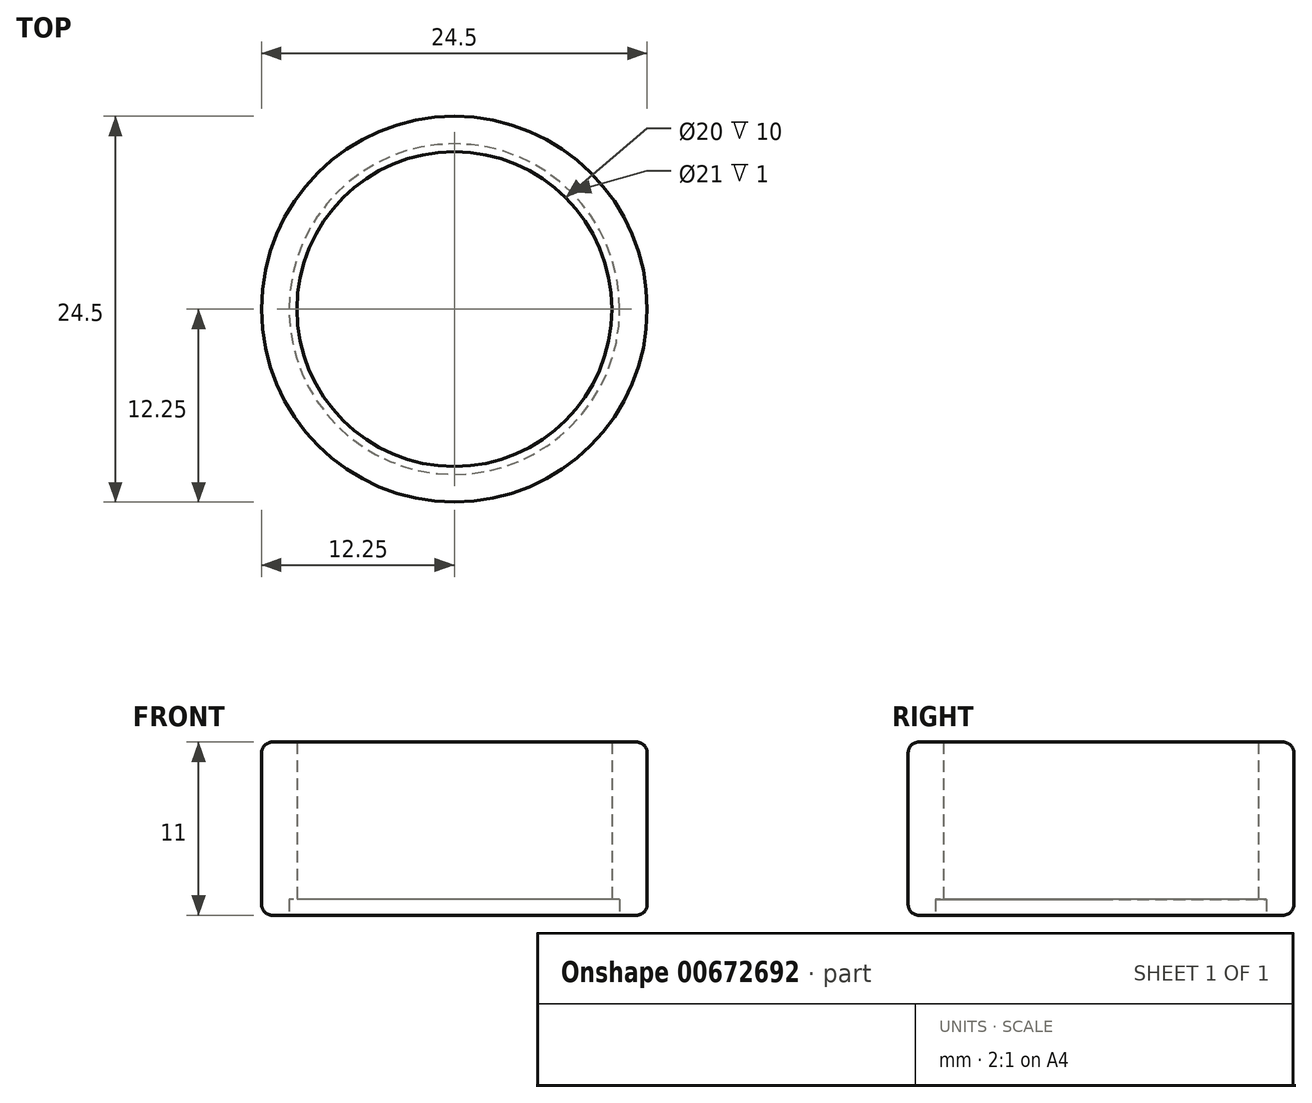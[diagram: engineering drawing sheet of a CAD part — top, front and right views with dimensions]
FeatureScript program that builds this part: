
annotation { "Feature Type Name" : "Feature", "Feature Type Description" : "" }
export const myFeature = defineFeature(function(context is Context, id is Id, definition is map)
    precondition{}
    {
        {
            var Q0;
            Q0=qCreatedBy(makeId("Top.planeOp"),FACE);
            var sketch = newSketch(context, id + "F0", { "sketchPlane" : qUnion([Q0])});
            skCircle(sketch, "E0", {"center": v(0, 0) * mm, "radius": 12.25 * mm});
            skCircle(sketch, "E1", {"center": v(0, 0) * mm, "radius": 10.5 * mm});
            skCircle(sketch, "E2", {"center": v(0, 0) * mm, "radius": 10 * mm});
            skSolve(sketch);
        }
        {
            var Q0;
            Q0=makeQuery(id+"F0.imprint","IMPRINT",FACE,{"disambiguationData":[TD([[makeQuery(id+"F0.imprint","IMPRINT",EDGE,{"derivedFrom":sQuery(id+"F0.wireOp",EDGE,"E0")}),1.0]])]});
            var Q1;
            Q1=makeQuery(id+"F0.imprint","IMPRINT",FACE,{"disambiguationData":[TD([[makeQuery(id+"F0.imprint","IMPRINT",EDGE,{"derivedFrom":sQuery(id+"F0.wireOp",EDGE,"E1")}),1.0]])]});
            extrude(context, id + "F1", {"entities" : qUnion([Q0, Q1]), "depth" : 11 * mm, "offsetDistance" : 25 * mm});
        }
        {
            var Q0;
            Q0=makeQuery(id+"F0.imprint","IMPRINT",FACE,{"disambiguationData":[TD([[makeQuery(id+"F0.imprint","IMPRINT",EDGE,{"derivedFrom":sQuery(id+"F0.wireOp",EDGE,"E1")}),1.0]])]});
            extrude(context, id + "F2", {"entities" : qUnion([Q0]), "operationType" : NewBodyOperationType.REMOVE, "depth" : 1 * mm, "offsetDistance" : 25 * mm});
        }
        {
            var Q0;
            Q0=makeQuery(id+"F1.opExtrude","CAP_EDGE",EDGE,{"disambiguationData":[OSD([sQuery(id+"F0.wireOp",EDGE,"E0")])],"isStart":true});
            var Q1;
            Q1=makeQuery(id+"F1.opExtrude","CAP_EDGE",EDGE,{"disambiguationData":[OSD([sQuery(id+"F0.wireOp",EDGE,"E0")])],"isStart":false});
            fillet(context, id + "F3", {"entities" : qUnion([Q0, Q1]), "radius" : 0.7 * mm, "tangentPropagation" : true, "allowEdgeOverflow" : false});
        }
    });
